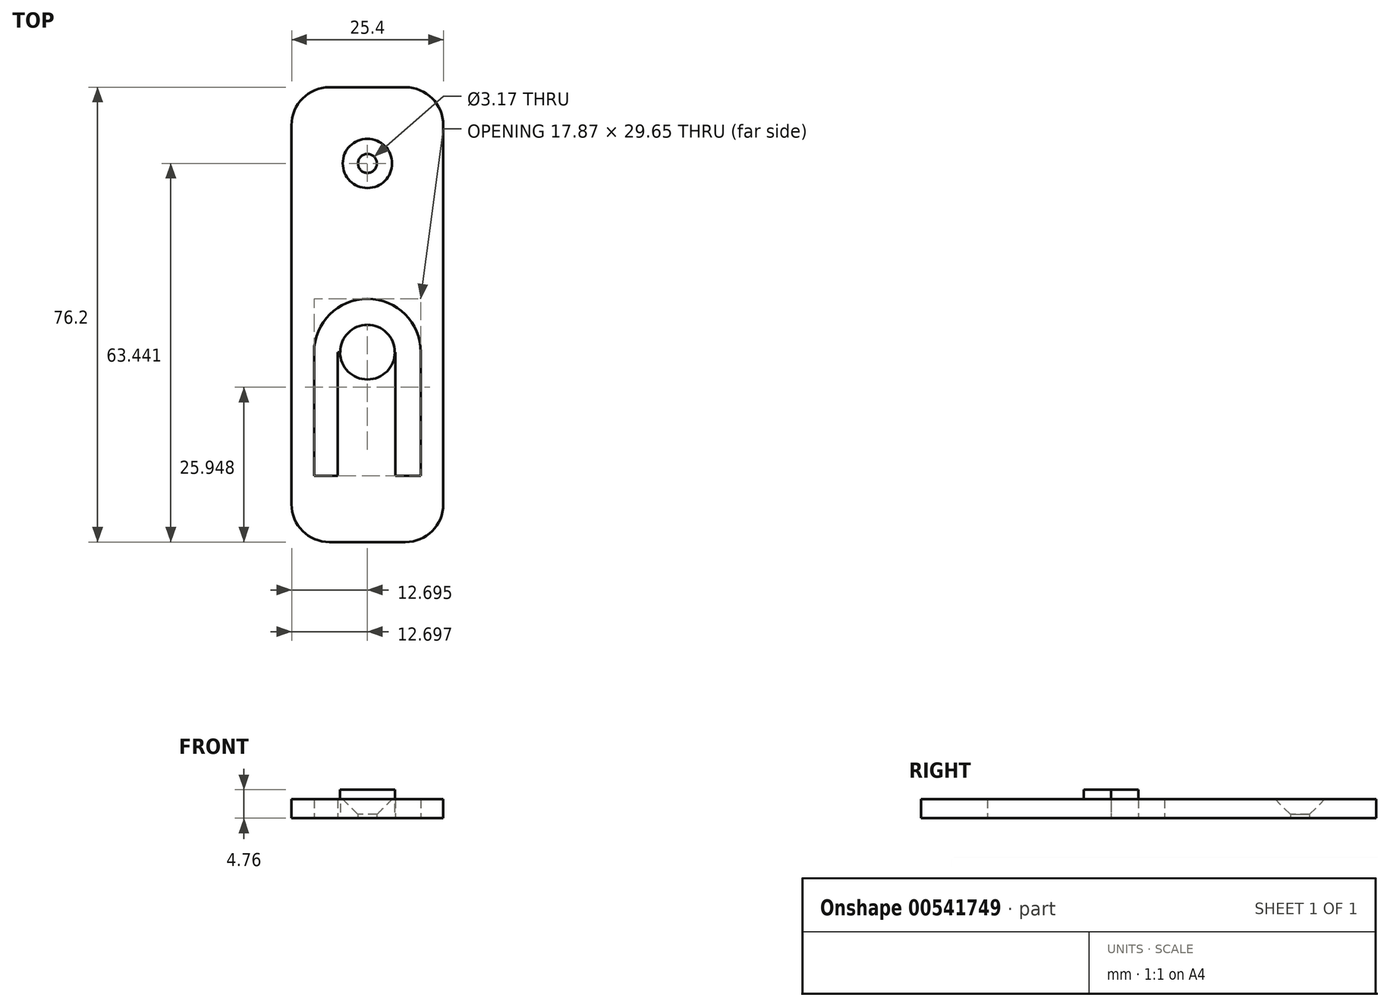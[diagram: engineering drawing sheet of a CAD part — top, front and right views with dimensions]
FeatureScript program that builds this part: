
annotation { "Feature Type Name" : "Feature", "Feature Type Description" : "" }
export const myFeature = defineFeature(function(context is Context, id is Id, definition is map)
    precondition{}
    {
        {
            var Q0;
            Q0=qCreatedBy(makeId("Top.planeOp"),FACE);
            var sketch = newSketch(context, id + "F0", { "sketchPlane" : qUnion([Q0])});
            skLineSegment(sketch, "E0.bottom", {"start": v(-31.74, -18.5) * mm, "end": v(-19.04, -18.5) * mm});
            skLineSegment(sketch, "E0.top", {"start": v(-31.74, 57.7) * mm, "end": v(-19.04, 57.7) * mm});
            skLineSegment(sketch, "E0.left", {"start": v(-38.1, -12.15) * mm, "end": v(-38.1, 51.35) * mm});
            skLineSegment(sketch, "E0.right", {"start": v(-12.7, -12.15) * mm, "end": v(-12.7, 51.35) * mm});
            skCircle(sketch, "E1", {"center": v(-25.4, 44.94) * mm, "radius": 1.59 * mm});
            skPoint(sketch, "E1.centerSnap0", {"position": v(-25.4, -18.5) * mm});
            skLineSegment(sketch, "E2.top", {"start": v(-30.36, 13.34) * mm, "end": v(-29.95, 13.34) * mm});
            skLineSegment(sketch, "E2.left", {"start": v(-30.36, -7.66) * mm, "end": v(-30.36, 13.34) * mm});
            skLineSegment(sketch, "E2.right", {"start": v(-20.71, -7.66) * mm, "end": v(-20.71, 13.34) * mm});
            skArc(sketch, "E3", {"start": v(-20.71, 13.34) * mm, "mid": v(-25.54, 18.16) * mm, "end": v(-30.36, 13.34) * mm});
            skLineSegment(sketch, "E4.bottom", {"start": v(-34.33, -7.38) * mm, "end": v(-30.36, -7.38) * mm});
            skLineSegment(sketch, "E4.left", {"start": v(-34.33, -7.38) * mm, "end": v(-34.33, 13.34) * mm});
            skLineSegment(sketch, "E4.right", {"start": v(-16.46, -7.38) * mm, "end": v(-16.46, 13.34) * mm});
            skArc(sketch, "E5", {"start": v(-16.46, 13.34) * mm, "mid": v(-25.4, 22.27) * mm, "end": v(-34.33, 13.34) * mm});
            skArc(sketch, "E6", {"start": v(-20.83, 13.34) * mm, "mid": v(-25.4, 17.9) * mm, "end": v(-29.95, 13.34) * mm});
            skPoint(sketch, "E7.visualSharp", {"position": v(-38.1, 57.7) * mm});
            skArc(sketch, "E7.filletArc", {"start": v(-31.74, 57.7) * mm, "mid": v(-36.23, 55.84) * mm, "end": v(-38.1, 51.35) * mm});
            skPoint(sketch, "E8.visualSharp", {"position": v(-12.7, 57.7) * mm});
            skArc(sketch, "E8.filletArc", {"start": v(-12.7, 51.35) * mm, "mid": v(-14.55, 55.84) * mm, "end": v(-19.04, 57.7) * mm});
            skPoint(sketch, "E9.visualSharp", {"position": v(-38.1, -18.5) * mm});
            skArc(sketch, "E9.filletArc", {"start": v(-38.1, -12.15) * mm, "mid": v(-36.23, -16.64) * mm, "end": v(-31.74, -18.5) * mm});
            skPoint(sketch, "E10.visualSharp", {"position": v(-12.7, -18.5) * mm});
            skArc(sketch, "E10.filletArc", {"start": v(-19.04, -18.5) * mm, "mid": v(-14.55, -16.64) * mm, "end": v(-12.7, -12.15) * mm});
            skLineSegment(sketch, "E11.trimOffspring", {"start": v(-20.71, -7.38) * mm, "end": v(-16.46, -7.38) * mm});
            skLineSegment(sketch, "E12.trimOffspring", {"start": v(-25.54, 13.34) * mm, "end": v(-25.4, 13.34) * mm});
            skLineSegment(sketch, "E13.trimOffspring", {"start": v(-20.83, 13.34) * mm, "end": v(-20.71, 13.34) * mm});
            skSolve(sketch);
        }
        {
            var Q0;
            Q0 = qSketchRegion(id + "F0", true);
            extrude(context, id + "F1", {"entities" : qUnion([Q0]), "depth" : 3.17 * mm, "offsetDistance" : 25.4 * mm});
        }
        {
            var Q0;
            Q0=makeQuery(id+"F1.opExtrude","CAP_FACE",FACE,{"disambiguationData":[OSD([sQuery(id+"F0.wireOp",EDGE,"E0.bottom"),sQuery(id+"F0.wireOp",EDGE,"E0.top"),sQuery(id+"F0.wireOp",EDGE,"E0.left"),sQuery(id+"F0.wireOp",EDGE,"E0.right"),sQuery(id+"F0.wireOp",EDGE,"E1"),sQuery(id+"F0.wireOp",EDGE,"E2.left"),sQuery(id+"F0.wireOp",EDGE,"E2.right"),sQuery(id+"F0.wireOp",EDGE,"E4.bottom"),sQuery(id+"F0.wireOp",EDGE,"E2.top"),sQuery(id+"F0.wireOp",EDGE,"E4.left"),sQuery(id+"F0.wireOp",EDGE,"E4.right"),sQuery(id+"F0.wireOp",EDGE,"E5"),sQuery(id+"F0.wireOp",EDGE,"E6"),sQuery(id+"F0.wireOp",EDGE,"E7.filletArc"),sQuery(id+"F0.wireOp",EDGE,"E8.filletArc"),sQuery(id+"F0.wireOp",EDGE,"E9.filletArc"),sQuery(id+"F0.wireOp",EDGE,"E10.filletArc"),sQuery(id+"F0.wireOp",EDGE,"E11.trimOffspring"),sQuery(id+"F0.wireOp",EDGE,"E13.trimOffspring")])],"isStart":false});
            var sketch = newSketch(context, id + "F2", { "sketchPlane" : qUnion([Q0])});
            skCircle(sketch, "E14", {"center": v(-25.4, 13.34) * mm, "radius": 4.6 * mm});
            skSolve(sketch);
        }
        {
            var Q0;
            {var subQ5=makeQuery(id+"F1.opExtrude","CAP_EDGE",EDGE,{"disambiguationData":[OSD([sQuery(id+"F0.wireOp",EDGE,"E6")])],"isStart":false});Q0=makeQuery(id+"F2.imprint","IMPRINT",FACE,{"disambiguationData":[TD([[makeQuery(id+"F2.imprint","IMPRINT",EDGE,{"derivedFrom":subQ5}),1.0]])]});}
            extrude(context, id + "F3", {"entities" : qUnion([Q0]), "operationType" : NewBodyOperationType.ADD, "depth" : 1.59 * mm, "offsetDistance" : 25.4 * mm});
        }
        {
            var Q0;
            Q0=makeQuery(id+"F1.opExtrude","CAP_EDGE",EDGE,{"disambiguationData":[OSD([sQuery(id+"F0.wireOp",EDGE,"E1")])],"isStart":false});
            chamfer(context, id + "F4", {"entities" : qUnion([Q0]), "width" : 2.54 * mm, "tangentPropagation" : true});
        }
    });
